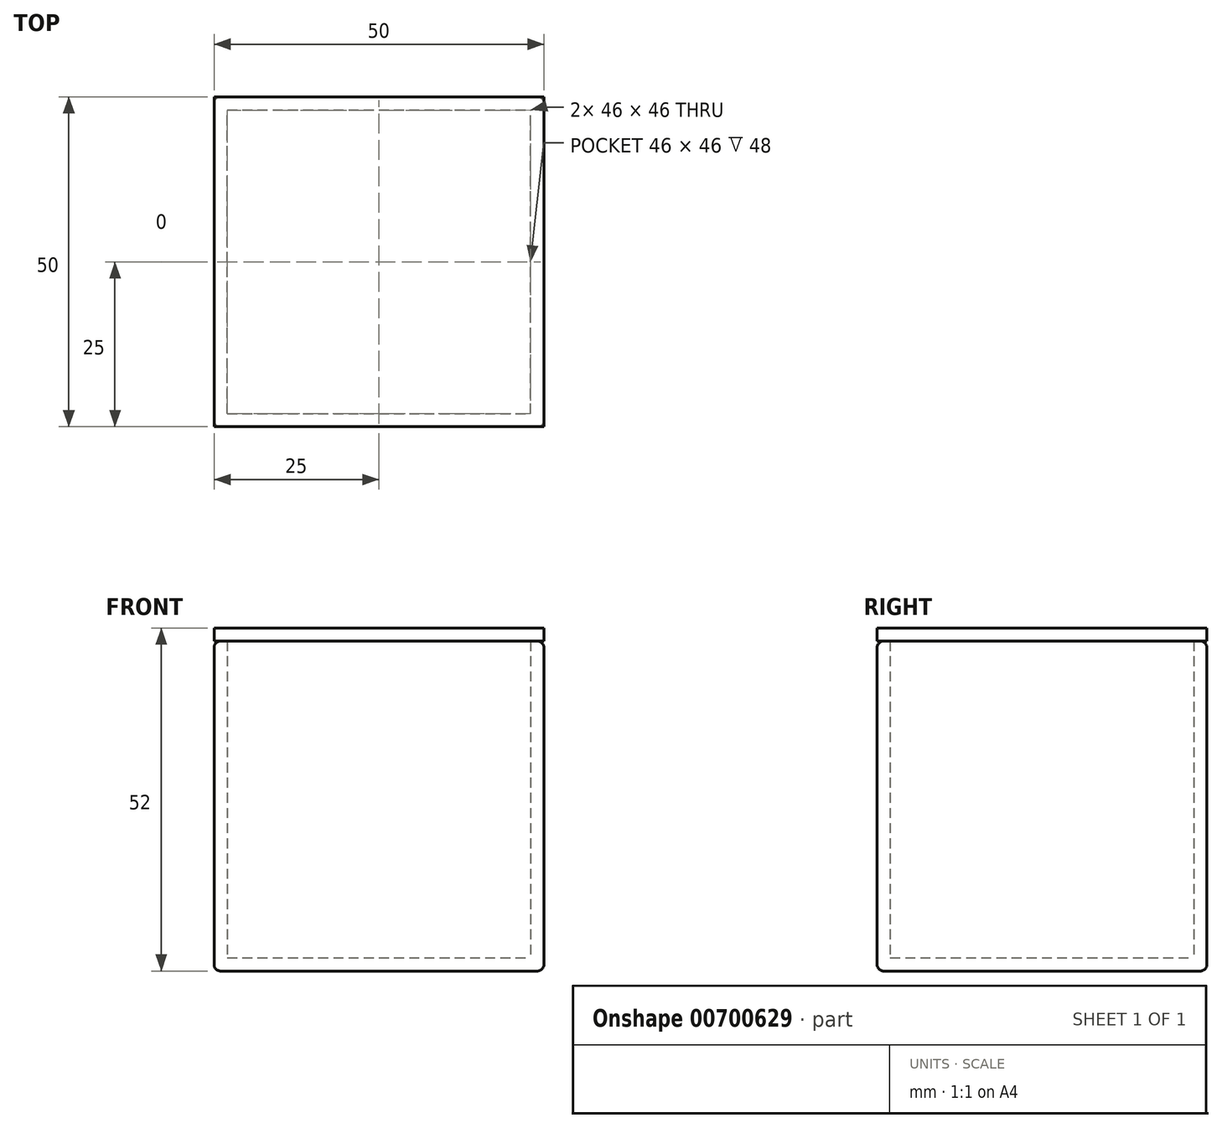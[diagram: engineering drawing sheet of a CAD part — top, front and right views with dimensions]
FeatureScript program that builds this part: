
annotation { "Feature Type Name" : "Feature", "Feature Type Description" : "" }
export const myFeature = defineFeature(function(context is Context, id is Id, definition is map)
    precondition{}
    {
        {
            var Q0;
            Q0=qCreatedBy(makeId("Front.planeOp"),FACE);
            var sketch = newSketch(context, id + "F0", { "sketchPlane" : qUnion([Q0])});
            skLineSegment(sketch, "E0.bottom", {"start": v(-25, 25) * mm, "end": v(25, 25) * mm});
            skLineSegment(sketch, "E0.top", {"start": v(-25, -25) * mm, "end": v(25, -25) * mm});
            skLineSegment(sketch, "E0.left", {"start": v(-25, 25) * mm, "end": v(-25, -25) * mm});
            skLineSegment(sketch, "E0.right", {"start": v(25, 25) * mm, "end": v(25, -25) * mm});
            skPoint(sketch, "E0.middle", {"position": v(0, 0) * mm});
            skSolve(sketch);
        }
        {
            var Q0;
            Q0=makeQuery(id+"F0.imprint","IMPRINT",FACE,{"disambiguationData":[TD([[makeQuery(id+"F0.imprint","IMPRINT",EDGE,{"derivedFrom":sQuery(id+"F0.wireOp",EDGE,"E0.bottom")}),-1.0]])]});
            extrude(context, id + "F1", {"entities" : qUnion([Q0]), "depth" : 50 * mm, "offsetDistance" : 25 * mm});
        }
        {
            var Q0;
            Q0=makeQuery(id+"F1.opExtrude","SWEPT_FACE",FACE,{"disambiguationData":[OSD([sQuery(id+"F0.wireOp",EDGE,"E0.bottom")])]});
            shell(context, id + "F2", {"entities" : qUnion([Q0]), "thickness" : 2 * mm});
        }
        {
            var Q0;
            Q0=makeQuery(id+"F1.opExtrude","CAP_EDGE",EDGE,{"disambiguationData":[OSD([sQuery(id+"F0.wireOp",EDGE,"E0.right")])],"isStart":false});
            var Q1;
            Q1=makeQuery(id+"F1.opExtrude","CAP_FACE",FACE,{"disambiguationData":[OSD([sQuery(id+"F0.wireOp",EDGE,"E0.bottom"),sQuery(id+"F0.wireOp",EDGE,"E0.top"),sQuery(id+"F0.wireOp",EDGE,"E0.left"),sQuery(id+"F0.wireOp",EDGE,"E0.right")])],"isStart":false});
            var Q2;
            Q2=makeQuery(id+"F1.opExtrude","SWEPT_FACE",FACE,{"disambiguationData":[OSD([sQuery(id+"F0.wireOp",EDGE,"E0.right")])]});
            var Q3;
            Q3=makeQuery(id+"F1.opExtrude","SWEPT_FACE",FACE,{"disambiguationData":[OSD([sQuery(id+"F0.wireOp",EDGE,"E0.left")])]});
            var Q4;
            Q4=makeQuery(id+"F1.opExtrude","CAP_FACE",FACE,{"disambiguationData":[OSD([sQuery(id+"F0.wireOp",EDGE,"E0.bottom"),sQuery(id+"F0.wireOp",EDGE,"E0.top"),sQuery(id+"F0.wireOp",EDGE,"E0.left"),sQuery(id+"F0.wireOp",EDGE,"E0.right")])],"isStart":true});
            fillet(context, id + "F3", {"entities" : qUnion([Q0, Q1, Q2, Q3, Q4]), "radius" : 1 * mm, "tangentPropagation" : true, "allowEdgeOverflow" : false});
        }
        {
            var Q0;
            Q0=qCreatedBy(makeId("Top.planeOp"),FACE);
            cPlane(context, id + "F4", {"entities" : qUnion([Q0]), "cplaneType" : CPlaneType.OFFSET, "offset" : 25 * mm, "width" : 150 * mm, "height" : 150 * mm});
        }
        {
            var Q0;
            Q0=qCreatedBy(id+"F4.planeOp",FACE);
            var sketch = newSketch(context, id + "F5", { "sketchPlane" : qUnion([Q0])});
            skLineSegment(sketch, "E1", {"start": v(0, 6.73) * mm, "end": v(0, -51.6) * mm, "construction": true});
            skLineSegment(sketch, "E2.0", {"start": v(-25, -49) * mm, "end": v(-25, -1) * mm, "construction": true});
            skLineSegment(sketch, "E3", {"start": v(-31, -25) * mm, "end": v(31.47, -25) * mm, "construction": true});
            skPoint(sketch, "E3.startSnap0", {"position": v(-25, -25) * mm});
            skLineSegment(sketch, "E4.bottom", {"start": v(-25, 0) * mm, "end": v(25, 0) * mm});
            skLineSegment(sketch, "E4.top", {"start": v(-25, -50) * mm, "end": v(25, -50) * mm});
            skLineSegment(sketch, "E4.left", {"start": v(-25, 0) * mm, "end": v(-25, -50) * mm});
            skLineSegment(sketch, "E4.right", {"start": v(25, 0) * mm, "end": v(25, -50) * mm});
            skPoint(sketch, "E4.middle", {"position": v(0, -25) * mm});
            skSolve(sketch);
        }
        {
            var Q0;
            Q0=makeQuery(id+"F5.imprint","IMPRINT",FACE,{"disambiguationData":[TD([[makeQuery(id+"F5.imprint","IMPRINT",EDGE,{"derivedFrom":sQuery(id+"F5.wireOp",EDGE,"E4.bottom")}),-1.0]])]});
            extrude(context, id + "F6", {"entities" : qUnion([Q0]), "depth" : 2 * mm, "offsetDistance" : 25 * mm});
        }
    });
